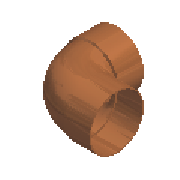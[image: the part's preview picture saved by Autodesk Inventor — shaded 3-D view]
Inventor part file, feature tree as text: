
AUTODESK INVENTOR PART (.ipt)
format: ipt  version: 2024 (Build 280153000, 153)  size: 248,320 bytes
history: native  units: mm (DEFAULTED — no unit token found)
features: other x10, sweep x2, revolve x2, plane x1
ambient origin geometry x8: Origin, YZ Plane, XZ Plane, XY Plane, X Axis, Y Axis, Z Axis, Center Point
bodies: Solid1 (feature_tree)
feature tree (15):
  plane  "Work Plane1"
  sweep  "Sweep1"
  revolve  "Revolution1"  [1 undecoded]
  revolve  "Revolution2"  [1 undecoded]
  sweep  "Sweep2"
  other  "Work Axis1"
  other  "Work Point1"
  other  "Work Point2"
  other  "Work Axis2"
  other  "Work Point3"
  other  "Work Point4"
  other  "Edición directa1"
  other  "Edición directa2"
  other  "Escala1"
  other  "Escala2"
note: 2 required parameter values undecoded (feature->parameter linkage not recoverable at this tier; creation-order binding heuristic only, values carry confidence <= 0.55)
